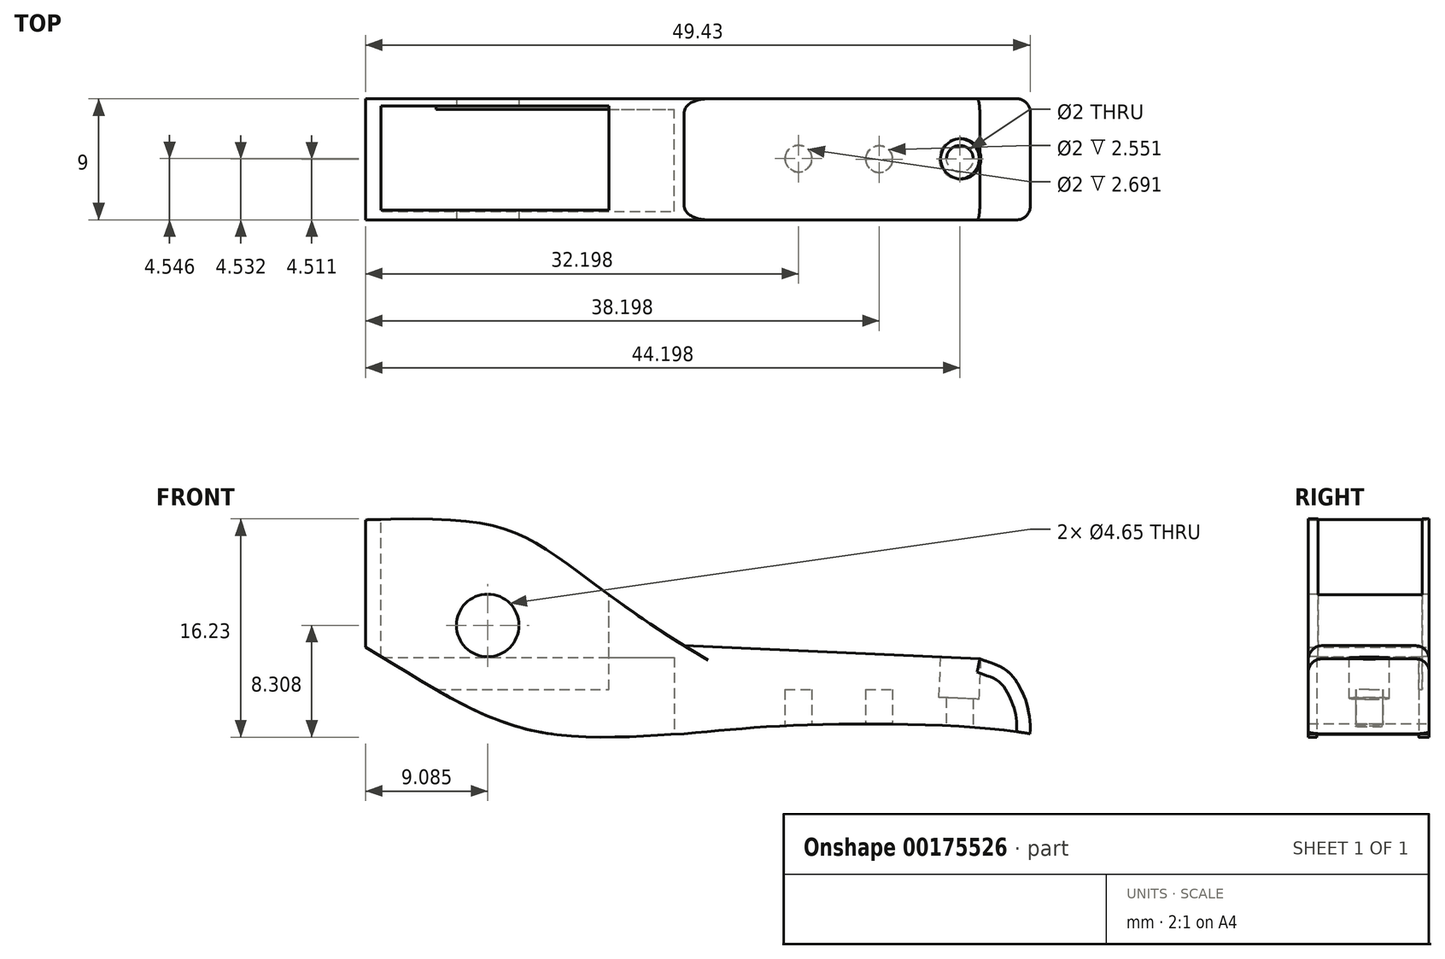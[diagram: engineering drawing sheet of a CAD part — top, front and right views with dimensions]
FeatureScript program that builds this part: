
annotation { "Feature Type Name" : "Feature", "Feature Type Description" : "" }
export const myFeature = defineFeature(function(context is Context, id is Id, definition is map)
    precondition{}
    {
        {
            var Q0;
            Q0=qCreatedBy(makeId("Front.planeOp"),FACE);
            var sketch = newSketch(context, id + "F0", { "sketchPlane" : qUnion([Q0])});
            skLineSegment(sketch, "E0", {"start": v(-18.11, 14.62) * mm, "end": v(-18.11, 5.15) * mm});
            skFitSpline(sketch, "E1", {"points": [v(-18.11, 14.62) * mm, v(-5.7, 13.04) * mm, v(5.6, 5.26) * mm], "startDerivative": vector(43.3, 1.46) * mm, "endDerivative": vector(32.79, -20.12) * mm});
            skFitSpline(sketch, "E2", {"points": [v(-18.11, 5.15) * mm, v(-6.1, -0.96) * mm, v(5.6, -1.29) * mm], "startDerivative": vector(24.76, -14.65) * mm, "endDerivative": vector(22.2, 1.12) * mm});
            skLineSegment(sketch, "E3", {"start": v(-5.7, 13.04) * mm, "end": v(-6.1, -0.96) * mm, "construction": true});
            skFitSpline(sketch, "E4", {"points": [v(5.6, -1.29) * mm, v(15.63, -0.6) * mm, v(31.3, -1.29) * mm], "startDerivative": vector(20.89, 1.84) * mm, "endDerivative": vector(17.9, -3.47) * mm});
            skLineSegment(sketch, "E5", {"start": v(5.6, 5.26) * mm, "end": v(27.57, 4.28) * mm});
            skFitSpline(sketch, "E6", {"points": [v(27.57, 4.28) * mm, v(30.02, 2.98) * mm, v(31.3, -1.29) * mm], "startDerivative": vector(8.93, -3.19) * mm, "endDerivative": vector(-1.08, -8.77) * mm});
            skLineSegment(sketch, "E7", {"start": v(-18.11, 14.62) * mm, "end": v(31.89, 14.62) * mm, "construction": true});
            skLineSegment(sketch, "E8", {"start": v(31.89, 14.62) * mm, "end": v(31.3, -1.29) * mm, "construction": true});
            skSolve(sketch);
        }
        {
            var Q0;
            Q0=qSketchRegion(id+"F0",true);
            extrude(context, id + "F1", {"entities" : qUnion([Q0]), "depth" : 9 * mm});
        }
        {
            var Q0;
            Q0=makeQuery(id+"F1.opExtrude","CAP_FACE",FACE,{"disambiguationData":[OSD([sQuery(id+"F0.wireOp",EDGE,"E0"),sQuery(id+"F0.wireOp",EDGE,"E1"),sQuery(id+"F0.wireOp",EDGE,"E2"),sQuery(id+"F0.wireOp",EDGE,"E4"),sQuery(id+"F0.wireOp",EDGE,"E5"),sQuery(id+"F0.wireOp",EDGE,"E6")])],"isStart":false});
            var sketch = newSketch(context, id + "F2", { "sketchPlane" : qUnion([Q0])});
            skCircle(sketch, "E9", {"center": v(-9.02, 6.77) * mm, "radius": 2.32 * mm});
            skSolve(sketch);
        }
        {
            var Q0;
            Q0=qSketchRegion(id+"F2",true);
            extrude(context, id + "F3", {"entities" : qUnion([Q0]), "operationType" : NewBodyOperationType.REMOVE, "oppositeDirection" : true, "depth" : 25 * mm});
        }
        {
            var Q0;
            Q0=makeQuery(id+"F1.opExtrude","CAP_EDGE",EDGE,{"disambiguationData":[OSD([sQuery(id+"F0.wireOp",EDGE,"E5")])],"isStart":false});
            var Q1;
            Q1=makeQuery(id+"F1.opExtrude","CAP_EDGE",EDGE,{"disambiguationData":[OSD([sQuery(id+"F0.wireOp",EDGE,"E5")])],"isStart":true});
            var Q2;
            Q2=makeQuery(id+"F1.opExtrude","CAP_EDGE",EDGE,{"disambiguationData":[OSD([sQuery(id+"F0.wireOp",EDGE,"E6")])],"isStart":false});
            var Q3;
            Q3=makeQuery(id+"F1.opExtrude","CAP_EDGE",EDGE,{"disambiguationData":[OSD([sQuery(id+"F0.wireOp",EDGE,"E6")])],"isStart":true});
            fillet(context, id + "F4", {"entities" : qUnion([Q0, Q1, Q2, Q3]), "radius" : 1 * mm, "tangentPropagation" : true, "allowEdgeOverflow" : false});
        }
        {
            var Q0;
            Q0=qCreatedBy(makeId("Top.planeOp"),FACE);
            cPlane(context, id + "F5", {"entities" : qUnion([Q0]), "cplaneType" : CPlaneType.OFFSET, "offset" : 3 * mm, "oppositeDirection" : true, "width" : 150 * mm, "height" : 150 * mm});
        }
        {
            var Q0;
            Q0=qCreatedBy(id+"F5.planeOp",FACE);
            cPlane(context, id + "F6", {"entities" : qUnion([Q0]), "cplaneType" : CPlaneType.OFFSET, "offset" : 25 * mm, "width" : 150 * mm, "height" : 150 * mm});
        }
        {
            var Q0;
            Q0=qCreatedBy(id+"F5.planeOp",FACE);
            var sketch = newSketch(context, id + "F7", { "sketchPlane" : qUnion([Q0])});
            skLineSegment(sketch, "E10.bottom", {"start": v(-17.4, -8.37) * mm, "end": v(4.86, -8.37) * mm});
            skLineSegment(sketch, "E10.top", {"start": v(-17.4, -0.78) * mm, "end": v(4.86, -0.78) * mm});
            skLineSegment(sketch, "E10.left", {"start": v(-17.4, -8.37) * mm, "end": v(-17.4, -0.78) * mm});
            skLineSegment(sketch, "E10.right", {"start": v(4.86, -8.37) * mm, "end": v(4.86, -0.78) * mm});
            skSolve(sketch);
        }
        {
            var Q0;
            Q0=qSketchRegion(id+"F7",true);
            extrude(context, id + "F8", {"entities" : qUnion([Q0]), "operationType" : NewBodyOperationType.REMOVE, "depth" : 7.4 * mm});
        }
        {
            var Q0;
            Q0=qCreatedBy(id+"F6.planeOp",FACE);
            var sketch = newSketch(context, id + "F9", { "sketchPlane" : qUnion([Q0])});
            skLineSegment(sketch, "E11.bottom", {"start": v(-16.96, -0.52) * mm, "end": v(0, -0.52) * mm});
            skLineSegment(sketch, "E11.top", {"start": v(-16.96, -8.27) * mm, "end": v(0, -8.27) * mm});
            skLineSegment(sketch, "E11.left", {"start": v(-16.96, -0.52) * mm, "end": v(-16.96, -8.27) * mm});
            skLineSegment(sketch, "E11.right", {"start": v(0, -0.52) * mm, "end": v(0, -8.27) * mm});
            skPoint(sketch, "E11.middle", {"position": v(-8.48, -4.4) * mm});
            skSolve(sketch);
        }
        {
            var Q0;
            Q0=qSketchRegion(id+"F9",true);
            extrude(context, id + "F10", {"entities" : qUnion([Q0]), "operationType" : NewBodyOperationType.REMOVE, "oppositeDirection" : true, "depth" : 20 * mm});
        }
        {
            var Q0;
            Q0=qCreatedBy(id+"F5.planeOp",FACE);
            var sketch = newSketch(context, id + "F11", { "sketchPlane" : qUnion([Q0])});
            skCircle(sketch, "E12", {"center": v(14.09, -4.45) * mm, "radius": 1 * mm});
            skCircle(sketch, "E13", {"center": v(20.09, -4.49) * mm, "radius": 1 * mm});
            skCircle(sketch, "E14", {"center": v(26.09, -4.47) * mm, "radius": 1 * mm});
            skLineSegment(sketch, "E15", {"start": v(5.59, -8.98) * mm, "end": v(5.59, 0) * mm, "construction": true});
            skLineSegment(sketch, "E16", {"start": v(5.59, 0) * mm, "end": v(5.59, -4.49) * mm, "construction": true});
            skLineSegment(sketch, "E17", {"start": v(5.59, -4.49) * mm, "end": v(34.6, -4.49) * mm, "construction": true});
            skLineSegment(sketch, "E18", {"start": v(26.09, -4.47) * mm, "end": v(31.59, -4.49) * mm, "construction": true});
            skSolve(sketch);
        }
        {
            var Q0;
            Q0=qSketchRegion(id+"F11",true);
            extrude(context, id + "F12", {"entities" : qUnion([Q0]), "operationType" : NewBodyOperationType.REMOVE, "depth" : 5 * mm});
        }
        {
            var Q0;
            Q0=makeQuery(id+"F1.opExtrude","SWEPT_FACE",FACE,{"disambiguationData":[OSD([sQuery(id+"F0.wireOp",EDGE,"E5")])]});
            var sketch = newSketch(context, id + "F13", { "sketchPlane" : qUnion([Q0])});
            skLineSegment(sketch, "E19", {"start": v(30.95, 0) * mm, "end": v(30.95, -8.92) * mm, "construction": true});
            skLineSegment(sketch, "E20", {"start": v(30.95, -8.92) * mm, "end": v(30.95, -4.46) * mm, "construction": true});
            skLineSegment(sketch, "E21", {"start": v(30.95, -4.46) * mm, "end": v(7.42, -4.46) * mm, "construction": true});
            skCircle(sketch, "E22", {"center": v(25.95, -4.46) * mm, "radius": 1.5 * mm});
            skSolve(sketch);
        }
        {
            var Q0;
            Q0=qSketchRegion(id+"F13",true);
            extrude(context, id + "F14", {"entities" : qUnion([Q0]), "operationType" : NewBodyOperationType.REMOVE, "oppositeDirection" : true, "depth" : 3 * mm});
        }
    });
